# Revit family: IS_Ceraflex_B5128_BIM_IT
name_source: partatom
category: Plumbing Fixtures
revit_build: Autodesk Revit MEP 2016 (Build: 20161004_0715(x64)
units: mm (PartAtom-declared; Revit-internal decimal feet)

## family parameters
Always vertical = No
Cut with Voids When Loaded = No
OmniClass Number = 23.45.55.17
OmniClass Title = Mixing Faucets
Part Type = Normal
Room Calculation Point = No
Round Connector Dimension = Use Diameter
Shared = No
Work Plane-Based = No

## types (1)
- B5128AA - CERAFLEX SNK MXR EXPSD TUB.SPT/235MM
    Accessori = www.idealstandard.it
    AltezzaNominale = 142 mm
    Assembly Code = C1030200
    Autore = Ideal Standard Italia
    BIMobject category = Taps & Mixers
    BOSUseNativeGeometries = 1
    Brand = Ideal Standard
    Brand url = http://www.idealstandard.co.uk
    Caratteristiche = Miscelatore monocomando a parete per lavello. Bocca d'erogazione orientabile. Raccordi ad S da 1/2", regolabili per interasse da 150+- 23 mm. Dotato di cartuccia da 40 mm con sistema Eko.
    CodiceABarre = 3800861056058
    Colore = Cromato
    Connessione = Installazione
    CostoDiSostituzione = 0 $
    Description = CERAPLUS - Miscelatore monocomando a parete per lavello. Bocca d'erogazione orientabile. Raccordi ad S da 1/2", regolabili per interasse da 150+- 23 mm. Dotato di cartuccia da 40 mm con sistema Eko.
    DescrizioneClassifcazioneUni2015 = Washbasin taps ?
    Dimensione = 142 x 220 x 296
    DurataGaranziaProdotti = 5
    EAN code = https://3800861056058
    Edition number = 1
    Finitura = Cromato
    Garanzia = Garanzia Idealstandard
    IFC Classification = Sanitary Terminal
    InformazioniDiProdotto = www.idealstandard.it/prodotti/html
    InformazioniGaranzia = www.idealstandard.it/garanzia.html
    Installation instructions = www.idealstandard.it/prodotti/html
    InstruzioniInstallazione = www.idealstandard.it/prodotti/html
    LarghezzaNominale = 220 mm
    LunghezzaNominale = 296 mm
    Manufacturer = www.idealstandard.it
    Manufacturer name = Ideal Standard
    Material main = Brass
    Materiale = Ottone
    Model = B5128AA
    NBS Reference Code = 35-79-95
    NBS Reference Description = Wash Basin And Trough Water Supply Fittings
    Nominal height = 141
    Nominal width = 0
    NumeroDiModello = B5128AA
    OmniClass Code = 23-31 11 00
    OmniClass Description = Faucets
    PesoNetto = 1,551 KG
    Product Guid = df174f2c-4e53-48c9-b0e8-02bd13a2000c
    Product SKU = B5128
    Product certification = http://www.idealstandard.it
    Product data url = https://bimobject.com
    Product family = CERAFLEX
    Product group = Kitchen Mixer
    Product name = CERAFLEX SINK MIXER EXPOSED TUB.SPT/235MM
    Product url = http://www.idealstandard.it
    QR code = http://bimobject.com
    Revisione = 1
    RiferimentoClassificazioneUni2015 = Pr_40_20_87_98
    Spazio = Interno
    Technical description = www.idealstandard.it/prodotti/html
    Telefono = 800 652 290
    URL = www.idealstandard.it
    Uniclass 1.4 Code = L8212
    Uniclass 1.4 Description = Fittings
    Uniclass 2.0 Code = PR-35-79-95
    Uniclass 2.0 Description = Wash Basin And Trough Water Supply Fittings
    Uniclass 2015 Code = Pr_40_20_87_96
    Uniclass 2015 Name = Washbasin manual water supply sets
    UnitaDurata = anni
    UnitaDurataGaranzia = anni
    UnitaLineare = milimetri
    UnitaVolume = Litri
    Versione = 1
    VersioneClassificazioneUni2015 = Products v1.1
    Weight Net (Kg) = 1.55

## geometry (parser evidence)
native form markers: Blend x4, Sweep x1
no freeform markers — native parametric forms only
